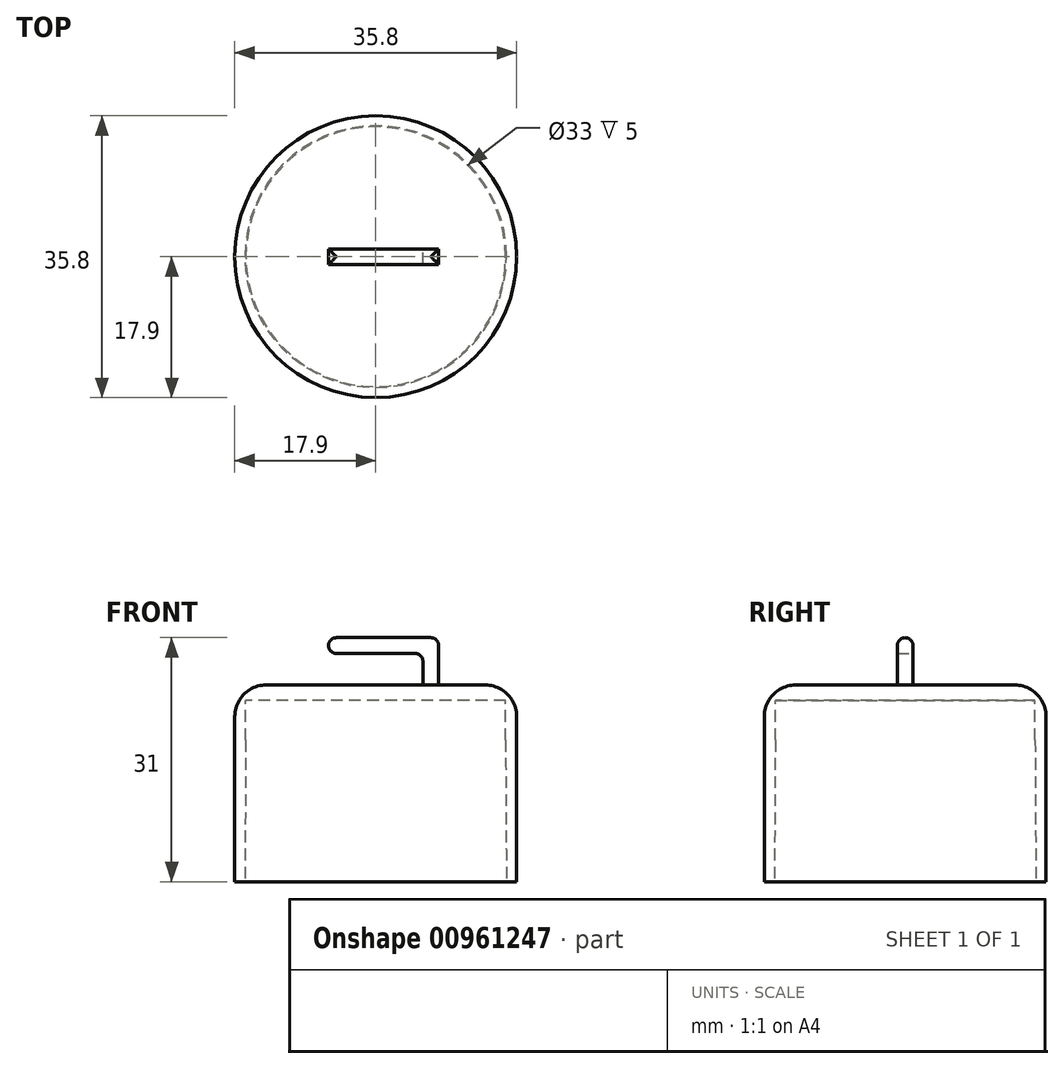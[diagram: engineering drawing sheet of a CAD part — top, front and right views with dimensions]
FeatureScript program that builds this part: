
annotation { "Feature Type Name" : "Feature", "Feature Type Description" : "" }
export const myFeature = defineFeature(function(context is Context, id is Id, definition is map)
    precondition{}
    {
        {
            var Q0;
            Q0=qCreatedBy(makeId("Top.planeOp"),FACE);
            var sketch = newSketch(context, id + "F0", { "sketchPlane" : qUnion([Q0])});
            skCircle(sketch, "E0", {"center": v(0, 0) * mm, "radius": 17.9 * mm});
            skCircle(sketch, "E1", {"center": v(0, 0) * mm, "radius": 16.5 * mm});
            skSolve(sketch);
        }
        {
            var Q0;
            Q0=makeQuery(id+"F0.imprint","IMPRINT",FACE,{"disambiguationData":[TD([[makeQuery(id+"F0.imprint","IMPRINT",EDGE,{"derivedFrom":sQuery(id+"F0.wireOp",EDGE,"E0")}),1.0]])]});
            extrude(context, id + "F1", {"entities" : qUnion([Q0]), "oppositeDirection" : true, "depth" : 25 * mm, "offsetDistance" : 25 * mm});
        }
        {
            var Q0;
            Q0=qCreatedBy(makeId("Front.planeOp"),FACE);
            var sketch = newSketch(context, id + "F2", { "sketchPlane" : qUnion([Q0])});
            skLineSegment(sketch, "E2.bottom", {"start": v(-41.01, 64.42) * mm, "end": v(41.01, 64.42) * mm});
            skLineSegment(sketch, "E2.top", {"start": v(-41.01, -64.42) * mm, "end": v(41.01, -64.42) * mm});
            skLineSegment(sketch, "E2.left", {"start": v(-41.01, 64.42) * mm, "end": v(-41.01, -64.42) * mm});
            skLineSegment(sketch, "E2.right", {"start": v(41.01, 64.42) * mm, "end": v(41.01, -64.42) * mm});
            skPoint(sketch, "E2.middle", {"position": v(0, 0) * mm});
            skSolve(sketch);
        }
        {
            var Q0;
            Q0=makeQuery(id+"F0.imprint","IMPRINT",FACE,{"disambiguationData":[TD([[makeQuery(id+"F0.imprint","IMPRINT",EDGE,{"derivedFrom":sQuery(id+"F0.wireOp",EDGE,"E1")}),1.0]])]});
            extrude(context, id + "F3", {"entities" : qUnion([Q0]), "operationType" : NewBodyOperationType.ADD, "oppositeDirection" : true, "depth" : 2 * mm, "offsetDistance" : 25 * mm});
        }
        {
            var Q0;
            Q0=makeQuery(id+"F2.imprint","IMPRINT",FACE,{"disambiguationData":[TD([[makeQuery(id+"F2.imprint","IMPRINT",EDGE,{"derivedFrom":sQuery(id+"F2.wireOp",EDGE,"E2.bottom")}),-1.0]])]});
            var sketch = newSketch(context, id + "F4", { "sketchPlane" : qUnion([Q0])});
            skLineSegment(sketch, "E3.bottom", {"start": v(6, 0) * mm, "end": v(8, 0) * mm});
            skLineSegment(sketch, "E3.top", {"start": v(6, 6) * mm, "end": v(8, 6) * mm});
            skLineSegment(sketch, "E3.left", {"start": v(6, 0) * mm, "end": v(6, 6) * mm});
            skLineSegment(sketch, "E3.right", {"start": v(8, 0) * mm, "end": v(8, 6) * mm});
            skLineSegment(sketch, "E4.bottom", {"start": v(6, 6) * mm, "end": v(-8, 6) * mm});
            skLineSegment(sketch, "E4.top", {"start": v(6, 4) * mm, "end": v(-8, 4) * mm});
            skLineSegment(sketch, "E4.left", {"start": v(6, 6) * mm, "end": v(6, 4) * mm});
            skLineSegment(sketch, "E4.right", {"start": v(-8, 6) * mm, "end": v(-8, 4) * mm});
            skLineSegment(sketch, "E5.bottom", {"start": v(-8, 4) * mm, "end": v(-6, 4) * mm});
            skLineSegment(sketch, "E5.top", {"start": v(-8, 1) * mm, "end": v(-6, 1) * mm});
            skLineSegment(sketch, "E5.left", {"start": v(-8, 4) * mm, "end": v(-8, 1) * mm});
            skLineSegment(sketch, "E5.right", {"start": v(-6, 4) * mm, "end": v(-6, 1) * mm});
            skLineSegment(sketch, "E6", {"start": v(-6, 4) * mm, "end": v(-6, 6) * mm});
            skLineSegment(sketch, "E7", {"start": v(-6, 4) * mm, "end": v(-4, 4) * mm});
            skSolve(sketch);
        }
        {
            var Q0;
            Q0=makeQuery(id+"F4.imprint","IMPRINT",FACE,{"disambiguationData":[TD([[makeQuery(id+"F4.imprint","IMPRINT",EDGE,{"derivedFrom":sQuery(id+"F4.wireOp",EDGE,"E3.bottom")}),1.0]])]});
            var Q1;
            Q1=makeQuery(id+"F4.imprint","IMPRINT",FACE,{"disambiguationData":[TD([[makeQuery(id+"F4.imprint","IMPRINT",EDGE,{"derivedFrom":sQuery(id+"F4.wireOp",EDGE,"E5.bottom")}),-1.0]])]});
            var Q2;
            Q2=makeQuery(id+"F4.imprint","IMPRINT",FACE,{"disambiguationData":[TD([[makeQuery(id+"F4.imprint","IMPRINT",EDGE,{"derivedFrom":sQuery(id+"F4.wireOp",EDGE,"E5.bottom")}),1.0]])]});
            var Q3;
            Q3=makeQuery(id+"F4.imprint","IMPRINT",FACE,{"disambiguationData":[TD([[makeQuery(id+"F4.imprint","IMPRINT",EDGE,{"derivedFrom":sQuery(id+"F4.wireOp",EDGE,"E4.top")}),-1.0]])]});
            extrude(context, id + "F5", {"entities" : qUnion([Q0, Q1, Q2, Q3]), "operationType" : NewBodyOperationType.ADD, "endBound" : BoundingType.SYMMETRIC, "depth" : 2 * mm, "offsetDistance" : 25 * mm});
        }
        {
            var Q0;
            Q0=makeQuery(id+"F5.opExtrude","SWEPT_EDGE",EDGE,{"disambiguationData":[OSD([sQuery(id+"F4.wireOp",EDGE,"E3.bottom"),sQuery(id+"F4.wireOp",EDGE,"E3.right")])]});
            var Q1;
            Q1=makeQuery(id+"F5.opExtrude","CAP_EDGE",EDGE,{"disambiguationData":[OSD([sQuery(id+"F4.wireOp",EDGE,"E3.bottom")])],"isStart":false});
            var Q2;
            Q2=makeQuery(id+"F5.opExtrude","CAP_EDGE",EDGE,{"disambiguationData":[OSD([sQuery(id+"F4.wireOp",EDGE,"E3.bottom")])],"isStart":true});
            var Q3;
            Q3=makeQuery(id+"F5.opExtrude","SWEPT_EDGE",EDGE,{"disambiguationData":[OSD([sQuery(id+"F4.wireOp",EDGE,"E3.left"),sQuery(id+"F4.wireOp",EDGE,"E4.top"),sQuery(id+"F4.wireOp",EDGE,"E4.left")])]});
            var Q4;
            Q4=makeQuery(id+"F5.opExtrude","SWEPT_EDGE",EDGE,{"disambiguationData":[OSD([sQuery(id+"F4.wireOp",EDGE,"E4.top"),sQuery(id+"F4.wireOp",EDGE,"E5.bottom"),sQuery(id+"F4.wireOp",EDGE,"E5.right")])]});
            var Q5;
            Q5=makeQuery(id+"F5.opExtrude","SWEPT_EDGE",EDGE,{"disambiguationData":[OSD([sQuery(id+"F4.wireOp",EDGE,"E3.top"),sQuery(id+"F4.wireOp",EDGE,"E3.right")])]});
            var Q6;
            Q6=makeQuery(id+"F5.opExtrude","SWEPT_EDGE",EDGE,{"disambiguationData":[OSD([sQuery(id+"F4.wireOp",EDGE,"E4.bottom"),sQuery(id+"F4.wireOp",EDGE,"E4.right")])]});
            var Q7;
            Q7=makeQuery(id+"F5.opExtrude","SWEPT_EDGE",EDGE,{"disambiguationData":[OSD([sQuery(id+"F4.wireOp",EDGE,"E3.bottom"),sQuery(id+"F4.wireOp",EDGE,"E3.left")])]});
            var Q8;
            Q8=makeQuery(id+"F5.opExtrude","SWEPT_EDGE",EDGE,{"disambiguationData":[OSD([sQuery(id+"F4.wireOp",EDGE,"E4.right"),sQuery(id+"F4.wireOp",EDGE,"E5.bottom"),sQuery(id+"F4.wireOp",EDGE,"E5.left"),sQuery(id+"F4.wireOp",EDGE,"8lF2bZsp-iQTd-zLWe-AxmJ-Sc5oBtxU9xXy")])]});
            var Q9;
            Q9=makeQuery(id+"F5.opExtrude","SWEPT_EDGE",EDGE,{"disambiguationData":[OSD([sQuery(id+"F4.wireOp",EDGE,"E5.top"),sQuery(id+"F4.wireOp",EDGE,"E5.left")])]});
            var Q10;
            Q10=makeQuery(id+"F5.opExtrude","SWEPT_EDGE",EDGE,{"disambiguationData":[OSD([sQuery(id+"F4.wireOp",EDGE,"E5.top"),sQuery(id+"F4.wireOp",EDGE,"E5.right")])]});
            var Q11;
            Q11=makeQuery(id+"F5.opExtrude","CAP_EDGE",EDGE,{"disambiguationData":[OSD([sQuery(id+"F4.wireOp",EDGE,"E3.top"),sQuery(id+"F4.wireOp",EDGE,"E4.bottom")])],"isStart":false});
            var Q12;
            Q12=makeQuery(id+"F5.opExtrude","CAP_EDGE",EDGE,{"disambiguationData":[OSD([sQuery(id+"F4.wireOp",EDGE,"E3.top"),sQuery(id+"F4.wireOp",EDGE,"E4.bottom")])],"isStart":true});
            fillet(context, id + "F6", {"entities" : qUnion([Q0, Q1, Q2, Q3, Q4, Q5, Q6, Q7, Q8, Q9, Q10, Q11, Q12]), "tangentPropagation" : true, "radius" : 1 * mm, "defaultsChanged" : false, "vertexSettings" : [], "allowEdgeOverflow" : false});
        }
        {
            var Q0;
            Q0=makeQuery(id+"F1.opExtrude","CAP_EDGE",EDGE,{"disambiguationData":[OSD([sQuery(id+"F0.wireOp",EDGE,"E0")])],"isStart":true});
            var Q1;
            Q1=makeQuery(id+"F3.opExtrude","CAP_EDGE",EDGE,{"disambiguationData":[OSD([sQuery(id+"F0.wireOp",EDGE,"E1")])],"isStart":false});
            fillet(context, id + "F7", {"entities" : qUnion([Q0, Q1]), "tangentPropagation" : true, "radius" : 4 * mm, "defaultsChanged" : true, "vertexSettings" : [], "allowEdgeOverflow" : false});
        }
        {
            var Q0;
            Q0=makeQuery(id+"F1.opExtrude","CAP_EDGE",EDGE,{"disambiguationData":[OSD([sQuery(id+"F0.wireOp",EDGE,"E1")])],"isStart":false});
            chamfer(context, id + "F8", {"entities" : qUnion([Q0]), "chamferType" : ChamferType.OFFSET_ANGLE, "width" : 18 * mm, "oppositeDirection" : true, "angle" : .35 * degree, "tangentPropagation" : true});
        }
    });
